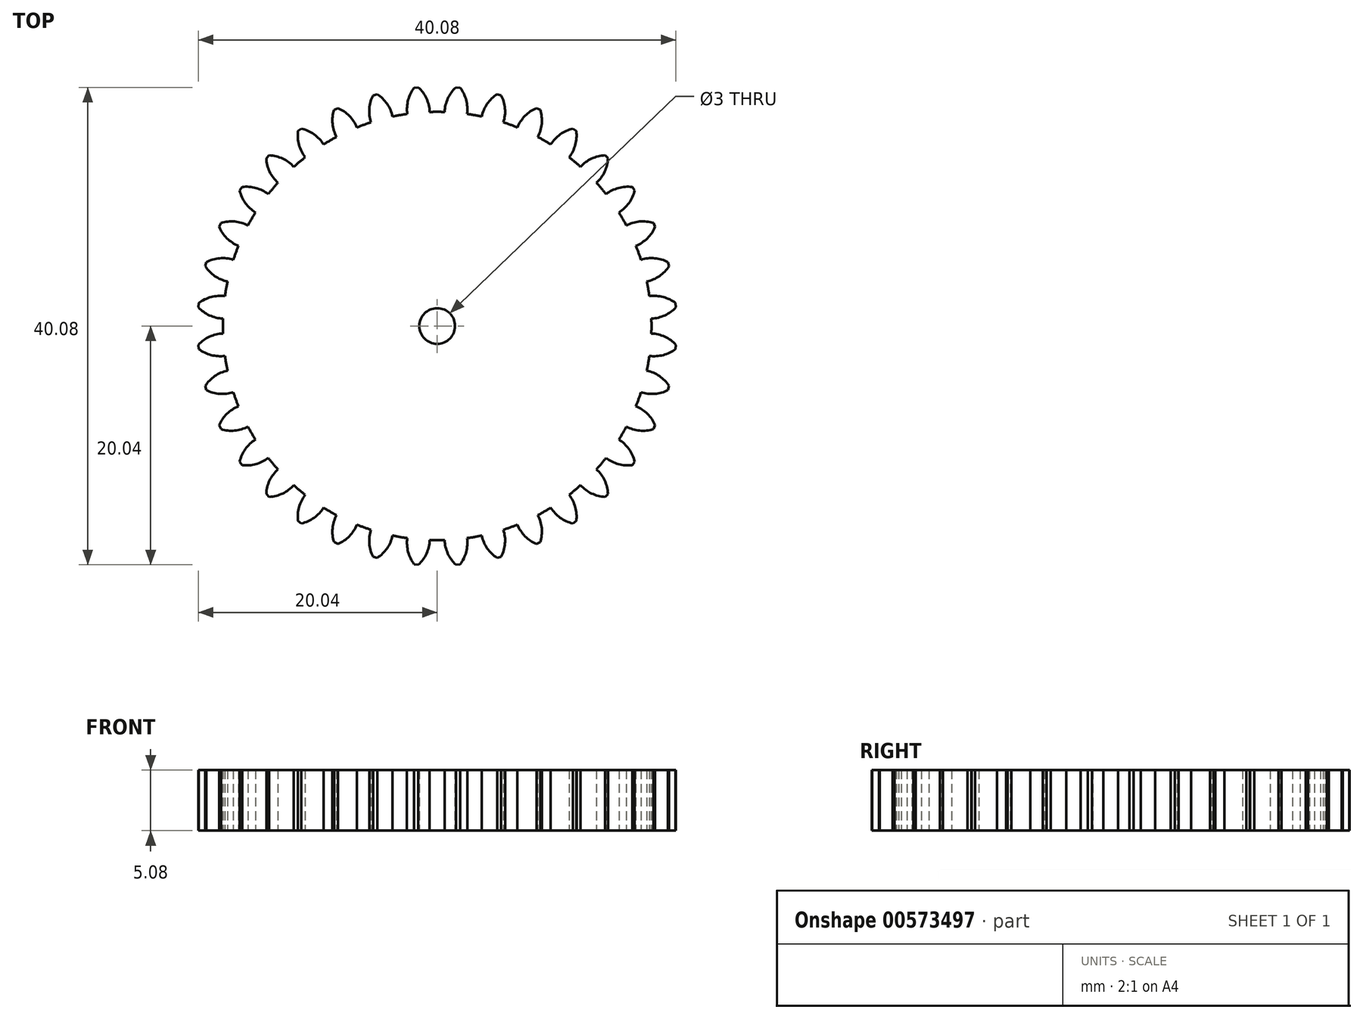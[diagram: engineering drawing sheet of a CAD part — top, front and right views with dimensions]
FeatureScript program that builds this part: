
annotation { "Feature Type Name" : "Feature", "Feature Type Description" : "" }
export const myFeature = defineFeature(function(context is Context, id is Id, definition is map)
    precondition{}
    {
        {
            var Q0;
            Q0=qCreatedBy(makeId("Top.planeOp"),FACE);
            var sketch = newSketch(context, id + "F0", { "sketchPlane" : qUnion([Q0])});
            skArc(sketch, "E0", {"start": v(-20.01, -1.93) * mm, "mid": v(-18.97, -2.44) * mm, "end": v(-17.81, -2.5) * mm});
            skLineSegment(sketch, "E1", {"start": v(-20.01, -1.93) * mm, "end": v(-20.04, -1.58) * mm});
            skArc(sketch, "E2", {"start": v(-20.04, -1.58) * mm, "mid": v(-19.1, -0.9) * mm, "end": v(-17.98, -0.63) * mm});
            skArc(sketch, "E3", {"start": v(-17.98, 0.63) * mm, "mid": v(-17.99, 0) * mm, "end": v(-17.98, -0.63) * mm});
            skArc(sketch, "E4.1.0", {"start": v(-17.81, -2.5) * mm, "mid": v(-17.71, -3.12) * mm, "end": v(-17.6, -3.74) * mm});
            skArc(sketch, "E4.1.1", {"start": v(-19.46, -5.03) * mm, "mid": v(-18.66, -4.2) * mm, "end": v(-17.6, -3.74) * mm});
            skLineSegment(sketch, "E4.1.2", {"start": v(-19.37, -5.37) * mm, "end": v(-19.46, -5.03) * mm});
            skArc(sketch, "E4.1.3", {"start": v(-19.37, -5.37) * mm, "mid": v(-18.26, -5.7) * mm, "end": v(-17.1, -5.56) * mm});
            skArc(sketch, "E4.2.0", {"start": v(-17.1, -5.56) * mm, "mid": v(-16.9, -6.15) * mm, "end": v(-16.68, -6.74) * mm});
            skArc(sketch, "E4.2.1", {"start": v(-18.3, -8.34) * mm, "mid": v(-17.65, -7.38) * mm, "end": v(-16.68, -6.74) * mm});
            skLineSegment(sketch, "E4.2.2", {"start": v(-18.15, -8.66) * mm, "end": v(-18.3, -8.34) * mm});
            skArc(sketch, "E4.2.3", {"start": v(-18.15, -8.66) * mm, "mid": v(-17, -8.78) * mm, "end": v(-15.88, -8.44) * mm});
            skArc(sketch, "E4.3.0", {"start": v(-15.88, -8.44) * mm, "mid": v(-15.58, -9) * mm, "end": v(-15.25, -9.53) * mm});
            skArc(sketch, "E4.3.1", {"start": v(-16.57, -11.39) * mm, "mid": v(-16.1, -10.33) * mm, "end": v(-15.25, -9.53) * mm});
            skLineSegment(sketch, "E4.3.2", {"start": v(-16.37, -11.67) * mm, "end": v(-16.57, -11.39) * mm});
            skArc(sketch, "E4.3.3", {"start": v(-16.37, -11.67) * mm, "mid": v(-15.2, -11.6) * mm, "end": v(-14.17, -11.07) * mm});
            skArc(sketch, "E4.4.0", {"start": v(-14.17, -11.07) * mm, "mid": v(-13.78, -11.56) * mm, "end": v(-13.37, -12.03) * mm});
            skArc(sketch, "E4.4.1", {"start": v(-14.34, -14.1) * mm, "mid": v(-14.06, -12.97) * mm, "end": v(-13.37, -12.03) * mm});
            skLineSegment(sketch, "E4.4.2", {"start": v(-14.1, -14.34) * mm, "end": v(-14.34, -14.1) * mm});
            skArc(sketch, "E4.4.3", {"start": v(-14.1, -14.34) * mm, "mid": v(-12.97, -14.06) * mm, "end": v(-12.03, -13.37) * mm});
            skArc(sketch, "E4.5.0", {"start": v(-12.03, -13.37) * mm, "mid": v(-11.56, -13.78) * mm, "end": v(-11.07, -14.17) * mm});
            skArc(sketch, "E4.5.1", {"start": v(-11.67, -16.37) * mm, "mid": v(-11.6, -15.2) * mm, "end": v(-11.07, -14.17) * mm});
            skLineSegment(sketch, "E4.5.2", {"start": v(-11.39, -16.57) * mm, "end": v(-11.67, -16.37) * mm});
            skArc(sketch, "E4.5.3", {"start": v(-11.39, -16.57) * mm, "mid": v(-10.33, -16.1) * mm, "end": v(-9.53, -15.25) * mm});
            skArc(sketch, "E4.6.0", {"start": v(-9.53, -15.25) * mm, "mid": v(-9, -15.58) * mm, "end": v(-8.44, -15.88) * mm});
            skArc(sketch, "E4.6.1", {"start": v(-8.66, -18.15) * mm, "mid": v(-8.78, -17) * mm, "end": v(-8.44, -15.88) * mm});
            skLineSegment(sketch, "E4.6.2", {"start": v(-8.34, -18.3) * mm, "end": v(-8.66, -18.15) * mm});
            skArc(sketch, "E4.6.3", {"start": v(-8.34, -18.3) * mm, "mid": v(-7.38, -17.65) * mm, "end": v(-6.74, -16.68) * mm});
            skArc(sketch, "E4.7.0", {"start": v(-6.74, -16.68) * mm, "mid": v(-6.15, -16.9) * mm, "end": v(-5.56, -17.1) * mm});
            skArc(sketch, "E4.7.1", {"start": v(-5.37, -19.37) * mm, "mid": v(-5.7, -18.26) * mm, "end": v(-5.56, -17.1) * mm});
            skLineSegment(sketch, "E4.7.2", {"start": v(-5.03, -19.46) * mm, "end": v(-5.37, -19.37) * mm});
            skArc(sketch, "E4.7.3", {"start": v(-5.03, -19.46) * mm, "mid": v(-4.2, -18.66) * mm, "end": v(-3.74, -17.6) * mm});
            skArc(sketch, "E4.8.0", {"start": v(-3.74, -17.6) * mm, "mid": v(-3.12, -17.71) * mm, "end": v(-2.5, -17.81) * mm});
            skArc(sketch, "E4.8.1", {"start": v(-1.93, -20.01) * mm, "mid": v(-2.44, -18.97) * mm, "end": v(-2.5, -17.81) * mm});
            skLineSegment(sketch, "E4.8.2", {"start": v(-1.58, -20.04) * mm, "end": v(-1.93, -20.01) * mm});
            skArc(sketch, "E4.8.3", {"start": v(-1.58, -20.04) * mm, "mid": v(-0.9, -19.1) * mm, "end": v(-0.63, -17.98) * mm});
            skArc(sketch, "E4.9.0", {"start": v(-0.63, -17.98) * mm, "mid": v(0, -17.99) * mm, "end": v(0.63, -17.98) * mm});
            skArc(sketch, "E4.9.1", {"start": v(1.58, -20.04) * mm, "mid": v(0.9, -19.1) * mm, "end": v(0.63, -17.98) * mm});
            skLineSegment(sketch, "E4.9.2", {"start": v(1.93, -20.01) * mm, "end": v(1.58, -20.04) * mm});
            skArc(sketch, "E4.9.3", {"start": v(1.93, -20.01) * mm, "mid": v(2.44, -18.97) * mm, "end": v(2.5, -17.81) * mm});
            skArc(sketch, "E4.10.0", {"start": v(2.5, -17.81) * mm, "mid": v(3.12, -17.71) * mm, "end": v(3.74, -17.6) * mm});
            skArc(sketch, "E4.10.1", {"start": v(5.03, -19.46) * mm, "mid": v(4.2, -18.66) * mm, "end": v(3.74, -17.6) * mm});
            skLineSegment(sketch, "E4.10.2", {"start": v(5.37, -19.37) * mm, "end": v(5.03, -19.46) * mm});
            skArc(sketch, "E4.10.3", {"start": v(5.37, -19.37) * mm, "mid": v(5.7, -18.26) * mm, "end": v(5.56, -17.1) * mm});
            skArc(sketch, "E4.11.0", {"start": v(5.56, -17.1) * mm, "mid": v(6.15, -16.9) * mm, "end": v(6.74, -16.68) * mm});
            skArc(sketch, "E4.11.1", {"start": v(8.34, -18.3) * mm, "mid": v(7.38, -17.65) * mm, "end": v(6.74, -16.68) * mm});
            skLineSegment(sketch, "E4.11.2", {"start": v(8.66, -18.15) * mm, "end": v(8.34, -18.3) * mm});
            skArc(sketch, "E4.11.3", {"start": v(8.66, -18.15) * mm, "mid": v(8.78, -17) * mm, "end": v(8.44, -15.88) * mm});
            skArc(sketch, "E4.12.0", {"start": v(8.44, -15.88) * mm, "mid": v(9, -15.58) * mm, "end": v(9.53, -15.25) * mm});
            skArc(sketch, "E4.12.1", {"start": v(11.39, -16.57) * mm, "mid": v(10.33, -16.1) * mm, "end": v(9.53, -15.25) * mm});
            skLineSegment(sketch, "E4.12.2", {"start": v(11.67, -16.37) * mm, "end": v(11.39, -16.57) * mm});
            skArc(sketch, "E4.12.3", {"start": v(11.67, -16.37) * mm, "mid": v(11.6, -15.2) * mm, "end": v(11.07, -14.17) * mm});
            skArc(sketch, "E4.13.0", {"start": v(11.07, -14.17) * mm, "mid": v(11.56, -13.78) * mm, "end": v(12.03, -13.37) * mm});
            skArc(sketch, "E4.13.1", {"start": v(14.1, -14.34) * mm, "mid": v(12.97, -14.06) * mm, "end": v(12.03, -13.37) * mm});
            skLineSegment(sketch, "E4.13.2", {"start": v(14.34, -14.1) * mm, "end": v(14.1, -14.34) * mm});
            skArc(sketch, "E4.13.3", {"start": v(14.34, -14.1) * mm, "mid": v(14.06, -12.97) * mm, "end": v(13.37, -12.03) * mm});
            skArc(sketch, "E4.14.0", {"start": v(13.37, -12.03) * mm, "mid": v(13.78, -11.56) * mm, "end": v(14.17, -11.07) * mm});
            skArc(sketch, "E4.14.1", {"start": v(16.37, -11.67) * mm, "mid": v(15.2, -11.6) * mm, "end": v(14.17, -11.07) * mm});
            skLineSegment(sketch, "E4.14.2", {"start": v(16.57, -11.39) * mm, "end": v(16.37, -11.67) * mm});
            skArc(sketch, "E4.14.3", {"start": v(16.57, -11.39) * mm, "mid": v(16.1, -10.33) * mm, "end": v(15.25, -9.53) * mm});
            skArc(sketch, "E4.15.0", {"start": v(15.25, -9.53) * mm, "mid": v(15.58, -9) * mm, "end": v(15.88, -8.44) * mm});
            skArc(sketch, "E4.15.1", {"start": v(18.15, -8.66) * mm, "mid": v(17, -8.78) * mm, "end": v(15.88, -8.44) * mm});
            skLineSegment(sketch, "E4.15.2", {"start": v(18.3, -8.34) * mm, "end": v(18.15, -8.66) * mm});
            skArc(sketch, "E4.15.3", {"start": v(18.3, -8.34) * mm, "mid": v(17.65, -7.38) * mm, "end": v(16.68, -6.74) * mm});
            skArc(sketch, "E4.16.0", {"start": v(16.68, -6.74) * mm, "mid": v(16.9, -6.15) * mm, "end": v(17.1, -5.56) * mm});
            skArc(sketch, "E4.16.1", {"start": v(19.37, -5.37) * mm, "mid": v(18.26, -5.7) * mm, "end": v(17.1, -5.56) * mm});
            skLineSegment(sketch, "E4.16.2", {"start": v(19.46, -5.03) * mm, "end": v(19.37, -5.37) * mm});
            skArc(sketch, "E4.16.3", {"start": v(19.46, -5.03) * mm, "mid": v(18.66, -4.2) * mm, "end": v(17.6, -3.74) * mm});
            skArc(sketch, "E4.17.0", {"start": v(17.6, -3.74) * mm, "mid": v(17.71, -3.12) * mm, "end": v(17.81, -2.5) * mm});
            skArc(sketch, "E4.17.1", {"start": v(20.01, -1.93) * mm, "mid": v(18.97, -2.44) * mm, "end": v(17.81, -2.5) * mm});
            skLineSegment(sketch, "E4.17.2", {"start": v(20.04, -1.58) * mm, "end": v(20.01, -1.93) * mm});
            skArc(sketch, "E4.17.3", {"start": v(20.04, -1.58) * mm, "mid": v(19.1, -0.9) * mm, "end": v(17.98, -0.63) * mm});
            skArc(sketch, "E4.18.0", {"start": v(17.98, -0.63) * mm, "mid": v(17.99, 0) * mm, "end": v(17.98, 0.63) * mm});
            skArc(sketch, "E4.18.1", {"start": v(20.04, 1.58) * mm, "mid": v(19.1, 0.9) * mm, "end": v(17.98, 0.63) * mm});
            skLineSegment(sketch, "E4.18.2", {"start": v(20.01, 1.93) * mm, "end": v(20.04, 1.58) * mm});
            skArc(sketch, "E4.18.3", {"start": v(20.01, 1.93) * mm, "mid": v(18.97, 2.44) * mm, "end": v(17.81, 2.5) * mm});
            skArc(sketch, "E4.19.0", {"start": v(17.81, 2.5) * mm, "mid": v(17.71, 3.12) * mm, "end": v(17.6, 3.74) * mm});
            skArc(sketch, "E4.19.1", {"start": v(19.46, 5.03) * mm, "mid": v(18.66, 4.2) * mm, "end": v(17.6, 3.74) * mm});
            skLineSegment(sketch, "E4.19.2", {"start": v(19.37, 5.37) * mm, "end": v(19.46, 5.03) * mm});
            skArc(sketch, "E4.19.3", {"start": v(19.37, 5.37) * mm, "mid": v(18.26, 5.7) * mm, "end": v(17.1, 5.56) * mm});
            skArc(sketch, "E4.20.0", {"start": v(17.1, 5.56) * mm, "mid": v(16.9, 6.15) * mm, "end": v(16.68, 6.74) * mm});
            skArc(sketch, "E4.20.1", {"start": v(18.3, 8.34) * mm, "mid": v(17.65, 7.38) * mm, "end": v(16.68, 6.74) * mm});
            skLineSegment(sketch, "E4.20.2", {"start": v(18.15, 8.66) * mm, "end": v(18.3, 8.34) * mm});
            skArc(sketch, "E4.20.3", {"start": v(18.15, 8.66) * mm, "mid": v(17, 8.78) * mm, "end": v(15.88, 8.44) * mm});
            skArc(sketch, "E4.21.0", {"start": v(15.88, 8.44) * mm, "mid": v(15.58, 9) * mm, "end": v(15.25, 9.53) * mm});
            skArc(sketch, "E4.21.1", {"start": v(16.57, 11.39) * mm, "mid": v(16.1, 10.33) * mm, "end": v(15.25, 9.53) * mm});
            skLineSegment(sketch, "E4.21.2", {"start": v(16.37, 11.67) * mm, "end": v(16.57, 11.39) * mm});
            skArc(sketch, "E4.21.3", {"start": v(16.37, 11.67) * mm, "mid": v(15.2, 11.6) * mm, "end": v(14.17, 11.07) * mm});
            skArc(sketch, "E4.22.0", {"start": v(14.17, 11.07) * mm, "mid": v(13.78, 11.56) * mm, "end": v(13.37, 12.03) * mm});
            skArc(sketch, "E4.22.1", {"start": v(14.34, 14.1) * mm, "mid": v(14.06, 12.97) * mm, "end": v(13.37, 12.03) * mm});
            skLineSegment(sketch, "E4.22.2", {"start": v(14.1, 14.34) * mm, "end": v(14.34, 14.1) * mm});
            skArc(sketch, "E4.22.3", {"start": v(14.1, 14.34) * mm, "mid": v(12.97, 14.06) * mm, "end": v(12.03, 13.37) * mm});
            skArc(sketch, "E4.23.0", {"start": v(12.03, 13.37) * mm, "mid": v(11.56, 13.78) * mm, "end": v(11.07, 14.17) * mm});
            skArc(sketch, "E4.23.1", {"start": v(11.67, 16.37) * mm, "mid": v(11.6, 15.2) * mm, "end": v(11.07, 14.17) * mm});
            skLineSegment(sketch, "E4.23.2", {"start": v(11.39, 16.57) * mm, "end": v(11.67, 16.37) * mm});
            skArc(sketch, "E4.23.3", {"start": v(11.39, 16.57) * mm, "mid": v(10.33, 16.1) * mm, "end": v(9.53, 15.25) * mm});
            skArc(sketch, "E4.24.0", {"start": v(9.53, 15.25) * mm, "mid": v(9, 15.58) * mm, "end": v(8.44, 15.88) * mm});
            skArc(sketch, "E4.24.1", {"start": v(8.66, 18.15) * mm, "mid": v(8.78, 17) * mm, "end": v(8.44, 15.88) * mm});
            skLineSegment(sketch, "E4.24.2", {"start": v(8.34, 18.3) * mm, "end": v(8.66, 18.15) * mm});
            skArc(sketch, "E4.24.3", {"start": v(8.34, 18.3) * mm, "mid": v(7.38, 17.65) * mm, "end": v(6.74, 16.68) * mm});
            skArc(sketch, "E4.25.0", {"start": v(6.74, 16.68) * mm, "mid": v(6.15, 16.9) * mm, "end": v(5.56, 17.1) * mm});
            skArc(sketch, "E4.25.1", {"start": v(5.37, 19.37) * mm, "mid": v(5.7, 18.26) * mm, "end": v(5.56, 17.1) * mm});
            skLineSegment(sketch, "E4.25.2", {"start": v(5.03, 19.46) * mm, "end": v(5.37, 19.37) * mm});
            skArc(sketch, "E4.25.3", {"start": v(5.03, 19.46) * mm, "mid": v(4.2, 18.66) * mm, "end": v(3.74, 17.6) * mm});
            skArc(sketch, "E4.26.0", {"start": v(3.74, 17.6) * mm, "mid": v(3.12, 17.71) * mm, "end": v(2.5, 17.81) * mm});
            skArc(sketch, "E4.26.1", {"start": v(1.93, 20.01) * mm, "mid": v(2.44, 18.97) * mm, "end": v(2.5, 17.81) * mm});
            skLineSegment(sketch, "E4.26.2", {"start": v(1.58, 20.04) * mm, "end": v(1.93, 20.01) * mm});
            skArc(sketch, "E4.26.3", {"start": v(1.58, 20.04) * mm, "mid": v(0.9, 19.1) * mm, "end": v(0.63, 17.98) * mm});
            skArc(sketch, "E4.27.0", {"start": v(0.63, 17.98) * mm, "mid": v(0, 17.99) * mm, "end": v(-0.63, 17.98) * mm});
            skArc(sketch, "E4.27.1", {"start": v(-1.58, 20.04) * mm, "mid": v(-0.9, 19.1) * mm, "end": v(-0.63, 17.98) * mm});
            skLineSegment(sketch, "E4.27.2", {"start": v(-1.93, 20.01) * mm, "end": v(-1.58, 20.04) * mm});
            skArc(sketch, "E4.27.3", {"start": v(-1.93, 20.01) * mm, "mid": v(-2.44, 18.97) * mm, "end": v(-2.5, 17.81) * mm});
            skArc(sketch, "E4.28.0", {"start": v(-2.5, 17.81) * mm, "mid": v(-3.12, 17.71) * mm, "end": v(-3.74, 17.6) * mm});
            skArc(sketch, "E4.28.1", {"start": v(-5.03, 19.46) * mm, "mid": v(-4.2, 18.66) * mm, "end": v(-3.74, 17.6) * mm});
            skLineSegment(sketch, "E4.28.2", {"start": v(-5.37, 19.37) * mm, "end": v(-5.03, 19.46) * mm});
            skArc(sketch, "E4.28.3", {"start": v(-5.37, 19.37) * mm, "mid": v(-5.7, 18.26) * mm, "end": v(-5.56, 17.1) * mm});
            skArc(sketch, "E4.29.0", {"start": v(-5.56, 17.1) * mm, "mid": v(-6.15, 16.9) * mm, "end": v(-6.74, 16.68) * mm});
            skArc(sketch, "E4.29.1", {"start": v(-8.34, 18.3) * mm, "mid": v(-7.38, 17.65) * mm, "end": v(-6.74, 16.68) * mm});
            skLineSegment(sketch, "E4.29.2", {"start": v(-8.66, 18.15) * mm, "end": v(-8.34, 18.3) * mm});
            skArc(sketch, "E4.29.3", {"start": v(-8.66, 18.15) * mm, "mid": v(-8.78, 17) * mm, "end": v(-8.44, 15.88) * mm});
            skArc(sketch, "E4.30.0", {"start": v(-8.44, 15.88) * mm, "mid": v(-9, 15.58) * mm, "end": v(-9.53, 15.25) * mm});
            skArc(sketch, "E4.30.1", {"start": v(-11.39, 16.57) * mm, "mid": v(-10.33, 16.1) * mm, "end": v(-9.53, 15.25) * mm});
            skLineSegment(sketch, "E4.30.2", {"start": v(-11.67, 16.37) * mm, "end": v(-11.39, 16.57) * mm});
            skArc(sketch, "E4.30.3", {"start": v(-11.67, 16.37) * mm, "mid": v(-11.6, 15.2) * mm, "end": v(-11.07, 14.17) * mm});
            skArc(sketch, "E4.31.0", {"start": v(-11.07, 14.17) * mm, "mid": v(-11.56, 13.78) * mm, "end": v(-12.03, 13.37) * mm});
            skArc(sketch, "E4.31.1", {"start": v(-14.1, 14.34) * mm, "mid": v(-12.97, 14.06) * mm, "end": v(-12.03, 13.37) * mm});
            skLineSegment(sketch, "E4.31.2", {"start": v(-14.34, 14.1) * mm, "end": v(-14.1, 14.34) * mm});
            skArc(sketch, "E4.31.3", {"start": v(-14.34, 14.1) * mm, "mid": v(-14.06, 12.97) * mm, "end": v(-13.37, 12.03) * mm});
            skArc(sketch, "E4.32.0", {"start": v(-13.37, 12.03) * mm, "mid": v(-13.78, 11.56) * mm, "end": v(-14.17, 11.07) * mm});
            skArc(sketch, "E4.32.1", {"start": v(-16.37, 11.67) * mm, "mid": v(-15.2, 11.6) * mm, "end": v(-14.17, 11.07) * mm});
            skLineSegment(sketch, "E4.32.2", {"start": v(-16.57, 11.39) * mm, "end": v(-16.37, 11.67) * mm});
            skArc(sketch, "E4.32.3", {"start": v(-16.57, 11.39) * mm, "mid": v(-16.1, 10.33) * mm, "end": v(-15.25, 9.53) * mm});
            skArc(sketch, "E4.33.0", {"start": v(-15.25, 9.53) * mm, "mid": v(-15.58, 9) * mm, "end": v(-15.88, 8.44) * mm});
            skArc(sketch, "E4.33.1", {"start": v(-18.15, 8.66) * mm, "mid": v(-17, 8.78) * mm, "end": v(-15.88, 8.44) * mm});
            skLineSegment(sketch, "E4.33.2", {"start": v(-18.3, 8.34) * mm, "end": v(-18.15, 8.66) * mm});
            skArc(sketch, "E4.33.3", {"start": v(-18.3, 8.34) * mm, "mid": v(-17.65, 7.38) * mm, "end": v(-16.68, 6.74) * mm});
            skArc(sketch, "E4.34.0", {"start": v(-16.68, 6.74) * mm, "mid": v(-16.9, 6.15) * mm, "end": v(-17.1, 5.56) * mm});
            skArc(sketch, "E4.34.1", {"start": v(-19.37, 5.37) * mm, "mid": v(-18.26, 5.7) * mm, "end": v(-17.1, 5.56) * mm});
            skLineSegment(sketch, "E4.34.2", {"start": v(-19.46, 5.03) * mm, "end": v(-19.37, 5.37) * mm});
            skArc(sketch, "E4.34.3", {"start": v(-19.46, 5.03) * mm, "mid": v(-18.66, 4.2) * mm, "end": v(-17.6, 3.74) * mm});
            skArc(sketch, "E4.35.0", {"start": v(-17.6, 3.74) * mm, "mid": v(-17.71, 3.12) * mm, "end": v(-17.81, 2.5) * mm});
            skArc(sketch, "E4.35.1", {"start": v(-20.01, 1.93) * mm, "mid": v(-18.97, 2.44) * mm, "end": v(-17.81, 2.5) * mm});
            skLineSegment(sketch, "E4.35.2", {"start": v(-20.04, 1.58) * mm, "end": v(-20.01, 1.93) * mm});
            skArc(sketch, "E4.35.3", {"start": v(-20.04, 1.58) * mm, "mid": v(-19.1, 0.9) * mm, "end": v(-17.98, 0.63) * mm});
            skCircle(sketch, "E5", {"center": v(0, 0) * mm, "radius": 1.5 * mm});
            skSolve(sketch);
        }
        {
            var Q0;
            Q0=makeQuery(id+"F0.imprint","IMPRINT",FACE,{"disambiguationData":[TD([[makeQuery(id+"F0.imprint","IMPRINT",EDGE,{"derivedFrom":sQuery(id+"F0.wireOp",EDGE,"E0")}),1.0]])]});
            extrude(context, id + "F1", {"entities" : qUnion([Q0]), "depth" : 5.08 * mm, "offsetDistance" : 25 * mm});
        }
    });
